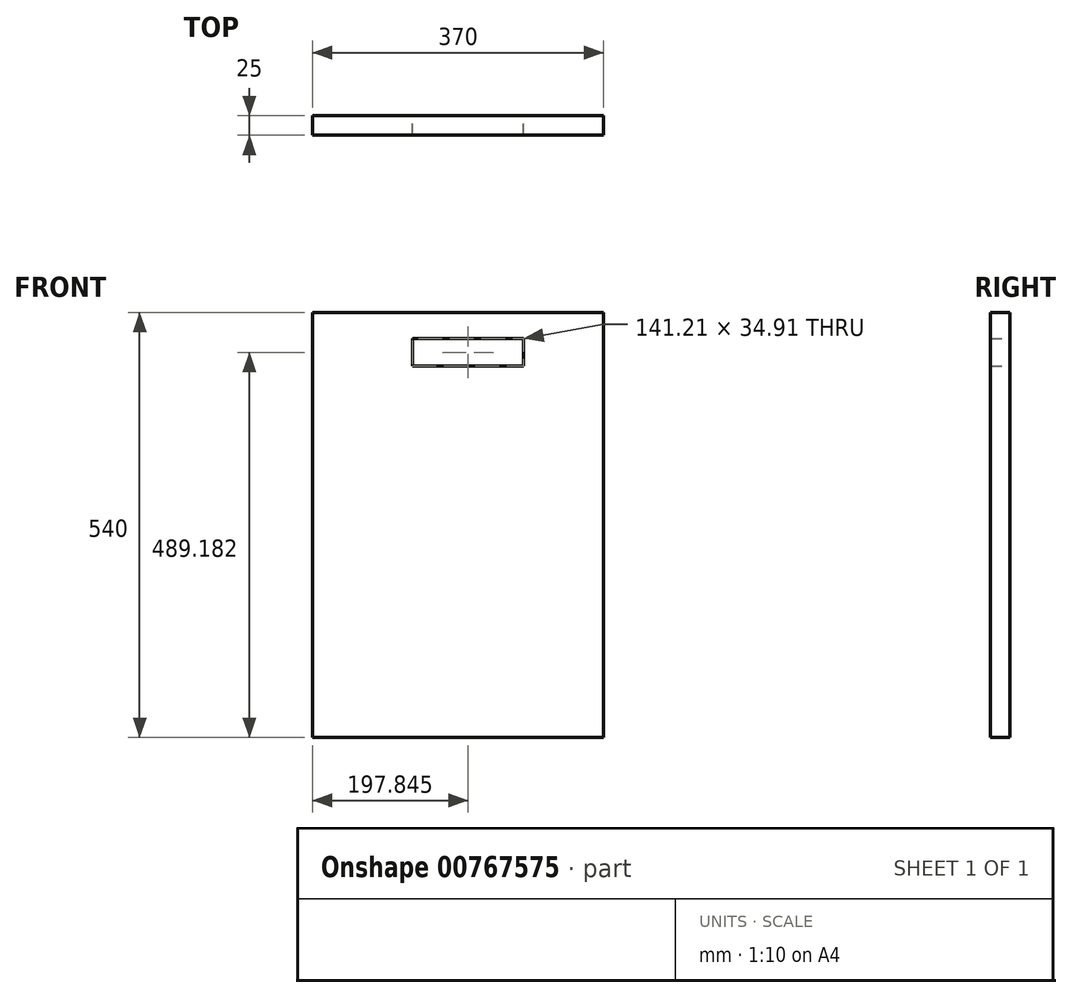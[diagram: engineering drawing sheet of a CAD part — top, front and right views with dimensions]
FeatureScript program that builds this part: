
annotation { "Feature Type Name" : "Feature", "Feature Type Description" : "" }
export const myFeature = defineFeature(function(context is Context, id is Id, definition is map)
    precondition{}
    {
        {
            var Q0;
            Q0=qCreatedBy(makeId("Front.planeOp"),FACE);
            var sketch = newSketch(context, id + "F0", { "sketchPlane" : qUnion([Q0])});
            skLineSegment(sketch, "E0.bottom", {"start": v(-191.96, 264.91) * mm, "end": v(178.04, 264.91) * mm});
            skLineSegment(sketch, "E0.top", {"start": v(-191.96, -275.09) * mm, "end": v(178.04, -275.09) * mm});
            skLineSegment(sketch, "E0.left", {"start": v(-191.96, 264.91) * mm, "end": v(-191.96, -275.09) * mm});
            skLineSegment(sketch, "E0.right", {"start": v(178.04, 264.91) * mm, "end": v(178.04, -275.09) * mm});
            skLineSegment(sketch, "E1.bottom", {"start": v(-64.72, 231.55) * mm, "end": v(76.49, 231.55) * mm});
            skLineSegment(sketch, "E1.top", {"start": v(-64.72, 196.64) * mm, "end": v(76.49, 196.64) * mm});
            skLineSegment(sketch, "E1.left", {"start": v(-64.72, 231.55) * mm, "end": v(-64.72, 196.64) * mm});
            skLineSegment(sketch, "E1.right", {"start": v(76.49, 231.55) * mm, "end": v(76.49, 196.64) * mm});
            skLineSegment(sketch, "E2", {"start": v(-6.96, -275.09) * mm, "end": v(-6.96, 264.91) * mm, "construction": true});
            skSolve(sketch);
        }
        {
            var Q0;
            Q0 = qSketchRegion(id + "F0", true);
            var Q1;
            Q1=makeQuery(id+"F0.imprint","IMPRINT",FACE,{"disambiguationData":[TD([[makeQuery(id+"F0.imprint","IMPRINT",EDGE,{"derivedFrom":sQuery(id+"F0.wireOp",EDGE,"E0.bottom")}),-1.0]])]});
            extrude(context, id + "F1", {"entities" : qUnion([Q0, Q1]), "depth" : 25 * mm, "offsetDistance" : 25 * mm});
        }
    });
